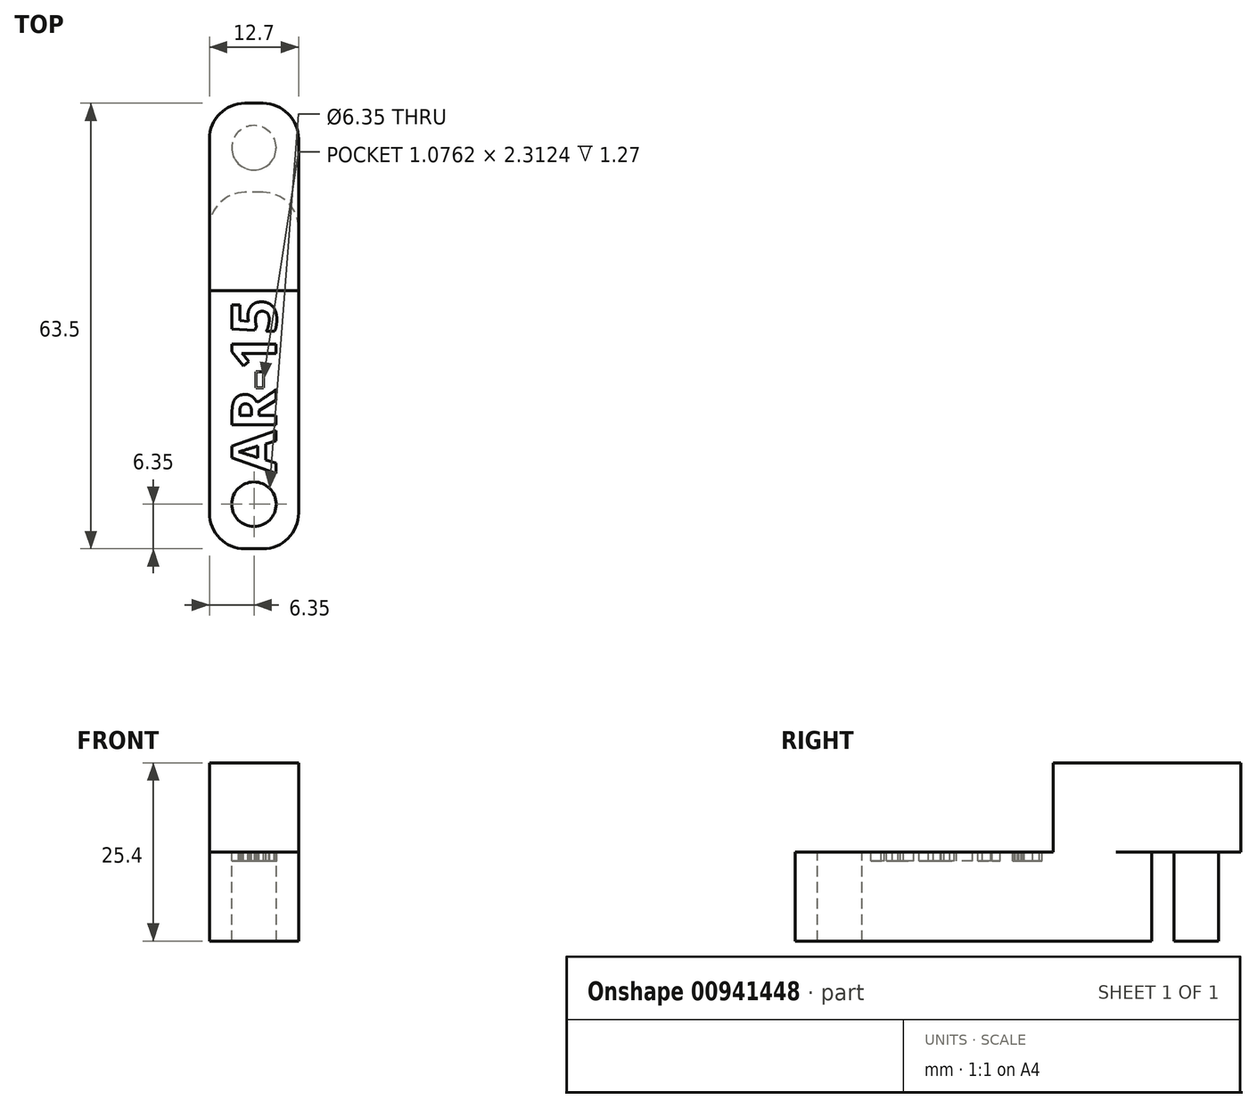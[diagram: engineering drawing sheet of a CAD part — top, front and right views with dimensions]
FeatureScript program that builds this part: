
annotation { "Feature Type Name" : "Feature", "Feature Type Description" : "" }
export const myFeature = defineFeature(function(context is Context, id is Id, definition is map)
    precondition{}
    {
        {
            var Q0;
            Q0=qCreatedBy(makeId("Top.planeOp"),FACE);
            var sketch = newSketch(context, id + "F0", { "sketchPlane" : qUnion([Q0])});
            skLineSegment(sketch, "E0.bottom", {"start": v(6.35, -25.4) * mm, "end": v(-6.35, -25.4) * mm});
            skLineSegment(sketch, "E0.top", {"start": v(6.35, 25.4) * mm, "end": v(-6.35, 25.4) * mm});
            skLineSegment(sketch, "E0.left", {"start": v(6.35, -25.4) * mm, "end": v(6.35, 25.4) * mm});
            skLineSegment(sketch, "E0.right", {"start": v(-6.35, -25.4) * mm, "end": v(-6.35, 25.4) * mm});
            skPoint(sketch, "E0.middle", {"position": v(0, 0) * mm});
            skSolve(sketch);
        }
        {
            var Q0;
            Q0 = qSketchRegion(id + "F0", true);
            extrude(context, id + "F1", {"entities" : qUnion([Q0]), "depth" : 12.7 * mm, "offsetDistance" : 25.4 * mm});
        }
        {
            var Q0;
            Q0=makeQuery(id+"F1.opExtrude","SWEPT_EDGE",EDGE,{"disambiguationData":[OSD([sQuery(id+"F0.wireOp",EDGE,"E0.top"),sQuery(id+"F0.wireOp",EDGE,"E0.right")])]});
            var Q1;
            Q1=makeQuery(id+"F1.opExtrude","SWEPT_EDGE",EDGE,{"disambiguationData":[OSD([sQuery(id+"F0.wireOp",EDGE,"E0.top"),sQuery(id+"F0.wireOp",EDGE,"E0.left")])]});
            fillet(context, id + "F2", {"entities" : qUnion([Q0, Q1]), "radius" : 5.08 * mm, "tangentPropagation" : true, "allowEdgeOverflow" : false});
        }
        {
            var Q0;
            Q0=makeQuery(id+"F1.opExtrude","CAP_FACE",FACE,{"disambiguationData":[OSD([sQuery(id+"F0.wireOp",EDGE,"E0.bottom"),sQuery(id+"F0.wireOp",EDGE,"E0.top"),sQuery(id+"F0.wireOp",EDGE,"E0.left"),sQuery(id+"F0.wireOp",EDGE,"E0.right")])],"isStart":false});
            var sketch = newSketch(context, id + "F3", { "sketchPlane" : qUnion([Q0])});
            skLineSegment(sketch, "E1.bottom", {"start": v(-6.35, 11.38) * mm, "end": v(6.35, 11.38) * mm});
            skLineSegment(sketch, "E1.top", {"start": v(-6.35, 38.1) * mm, "end": v(6.35, 38.1) * mm});
            skLineSegment(sketch, "E1.left", {"start": v(-6.35, 11.38) * mm, "end": v(-6.35, 38.1) * mm});
            skLineSegment(sketch, "E1.right", {"start": v(6.35, 11.38) * mm, "end": v(6.35, 38.1) * mm});
            skSolve(sketch);
        }
        {
            var Q0;
            {var subQ7=sQuery(id+"F3.wireOp",EDGE,"E1.bottom");Q0=makeQuery(id+"F3.imprint","IMPRINT",FACE,{"disambiguationData":[TD([[makeQuery(id+"F3.imprint","IMPRINT",EDGE,{"derivedFrom":subQ7}),1.0]])]});}
            var Q1;
            {var subQ6=sQuery(id+"F3.wireOp",EDGE,"E1.top");Q1=makeQuery(id+"F3.imprint","IMPRINT",FACE,{"disambiguationData":[TD([[makeQuery(id+"F3.imprint","IMPRINT",EDGE,{"derivedFrom":subQ6}),-1.0]])]});}
            extrude(context, id + "F4", {"entities" : qUnion([Q0, Q1]), "operationType" : NewBodyOperationType.ADD, "depth" : 12.7 * mm, "offsetDistance" : 25.4 * mm});
        }
        {
            var Q0;
            Q0=makeQuery(id+"F4.opExtrude","SWEPT_EDGE",EDGE,{"disambiguationData":[OSD([sQuery(id+"F3.wireOp",EDGE,"E1.top"),sQuery(id+"F3.wireOp",EDGE,"E1.left")])]});
            var Q1;
            Q1=makeQuery(id+"F4.opExtrude","SWEPT_EDGE",EDGE,{"disambiguationData":[OSD([sQuery(id+"F3.wireOp",EDGE,"E1.top"),sQuery(id+"F3.wireOp",EDGE,"E1.right")])]});
            fillet(context, id + "F5", {"entities" : qUnion([Q0, Q1]), "radius" : 5.08 * mm, "tangentPropagation" : true, "allowEdgeOverflow" : false});
        }
        {
            var Q0;
            Q0=makeQuery(id+"F4.opExtrude","CAP_FACE",FACE,{"disambiguationData":[OSD([sQuery(id+"F3.wireOp",EDGE,"E1.bottom"),sQuery(id+"F3.wireOp",EDGE,"E1.top"),sQuery(id+"F3.wireOp",EDGE,"E1.left"),sQuery(id+"F3.wireOp",EDGE,"E1.right")])],"isStart":true});
            var sketch = newSketch(context, id + "F6", { "sketchPlane" : qUnion([Q0])});
            skCircle(sketch, "E2", {"center": v(0, -31.75) * mm, "radius": 3.18 * mm});
            skSolve(sketch);
        }
        {
            var Q0;
            Q0=makeQuery(id+"F6.imprint","IMPRINT",FACE,{"disambiguationData":[TD([[makeQuery(id+"F6.imprint","IMPRINT",EDGE,{"derivedFrom":sQuery(id+"F6.wireOp",EDGE,"E2")}),1.0]])]});
            extrude(context, id + "F7", {"entities" : qUnion([Q0]), "operationType" : NewBodyOperationType.ADD, "depth" : 12.7 * mm, "offsetDistance" : 25.4 * mm});
        }
        {
            var Q0;
            Q0=makeQuery(id+"F1.opExtrude","SWEPT_EDGE",EDGE,{"disambiguationData":[OSD([sQuery(id+"F0.wireOp",EDGE,"E0.bottom"),sQuery(id+"F0.wireOp",EDGE,"E0.right")])]});
            var Q1;
            Q1=makeQuery(id+"F1.opExtrude","SWEPT_EDGE",EDGE,{"disambiguationData":[OSD([sQuery(id+"F0.wireOp",EDGE,"E0.bottom"),sQuery(id+"F0.wireOp",EDGE,"E0.left")])]});
            fillet(context, id + "F8", {"entities" : qUnion([Q0, Q1]), "radius" : 5.08 * mm, "tangentPropagation" : true, "allowEdgeOverflow" : false});
        }
        {
            var Q0;
            Q0=makeQuery(id+"F1.opExtrude","CAP_FACE",FACE,{"disambiguationData":[OSD([sQuery(id+"F0.wireOp",EDGE,"E0.bottom"),sQuery(id+"F0.wireOp",EDGE,"E0.top"),sQuery(id+"F0.wireOp",EDGE,"E0.left"),sQuery(id+"F0.wireOp",EDGE,"E0.right")])],"isStart":false});
            var sketch = newSketch(context, id + "F9", { "sketchPlane" : qUnion([Q0])});
            skCircle(sketch, "E3", {"center": v(0, -19.05) * mm, "radius": 3.18 * mm});
            skSolve(sketch);
        }
        {
            var Q0;
            Q0=makeQuery(id+"F9.imprint","IMPRINT",FACE,{"disambiguationData":[TD([[makeQuery(id+"F9.imprint","IMPRINT",EDGE,{"derivedFrom":sQuery(id+"F9.wireOp",EDGE,"E3")}),1.0]])]});
            extrude(context, id + "F10", {"entities" : qUnion([Q0]), "operationType" : NewBodyOperationType.REMOVE, "endBound" : BoundingType.UP_TO_NEXT, "oppositeDirection" : true, "depth" : 25.4 * mm, "offsetDistance" : 25.4 * mm});
        }
        {
            var Q0;
            Q0=makeQuery(id+"F1.opExtrude","CAP_FACE",FACE,{"disambiguationData":[OSD([sQuery(id+"F0.wireOp",EDGE,"E0.bottom"),sQuery(id+"F0.wireOp",EDGE,"E0.top"),sQuery(id+"F0.wireOp",EDGE,"E0.left"),sQuery(id+"F0.wireOp",EDGE,"E0.right")])],"isStart":false});
            var sketch = newSketch(context, id + "F11", { "sketchPlane" : qUnion([Q0])});
            skText(sketch, "E4", { "text": "AR-15", "fontName": "OpenSans-Bold.ttf"});
            const initialGuessF11  = {"E4": [0.00317, -0.01463, 0, 1, 0.00635]};
            skSetInitialGuess(sketch, initialGuessF11);
            skSolve(sketch);
        }
        {
            var Q0;
            Q0 = qSketchRegion(id + "F11", true);
            extrude(context, id + "F12", {"entities" : qUnion([Q0]), "operationType" : NewBodyOperationType.REMOVE, "oppositeDirection" : true, "depth" : 1.27 * mm, "offsetDistance" : 25.4 * mm});
        }
    });
